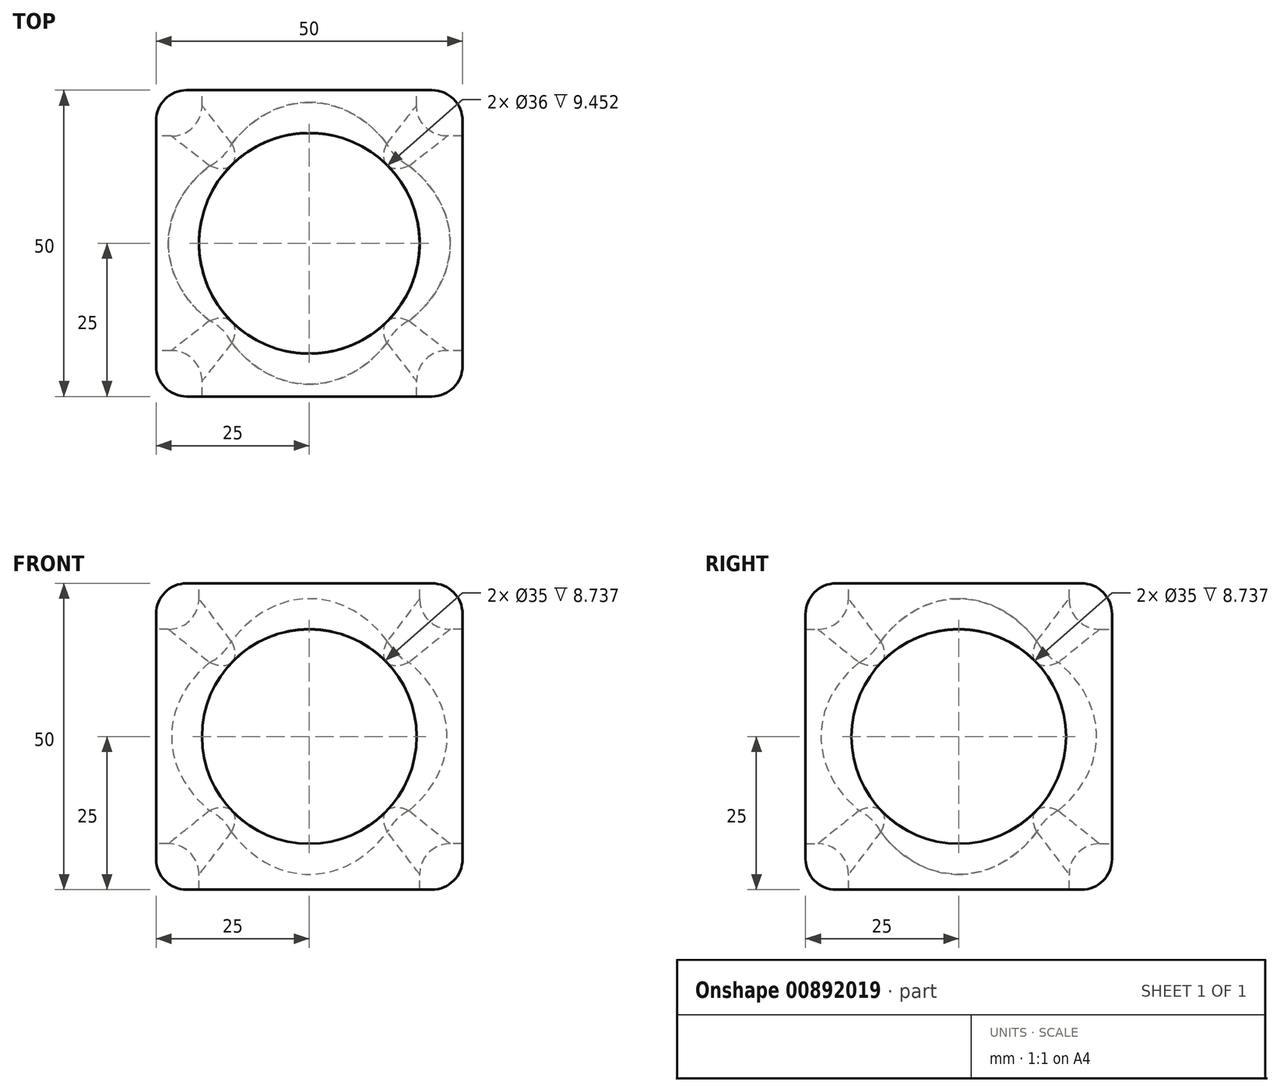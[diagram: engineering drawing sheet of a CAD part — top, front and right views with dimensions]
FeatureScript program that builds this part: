
annotation { "Feature Type Name" : "Feature", "Feature Type Description" : "" }
export const myFeature = defineFeature(function(context is Context, id is Id, definition is map)
    precondition{}
    {
        {
            var Q0;
            Q0=qCreatedBy(makeId("Top.planeOp"),FACE);
            var sketch = newSketch(context, id + "F0", { "sketchPlane" : qUnion([Q0])});
            skLineSegment(sketch, "E0.bottom", {"start": v(0, 0) * mm, "end": v(50, 0) * mm});
            skLineSegment(sketch, "E0.top", {"start": v(0, 50) * mm, "end": v(50, 50) * mm});
            skLineSegment(sketch, "E0.left", {"start": v(0, 0) * mm, "end": v(0, 50) * mm});
            skLineSegment(sketch, "E0.right", {"start": v(50, 0) * mm, "end": v(50, 50) * mm});
            skSolve(sketch);
        }
        {
            var Q0;
            Q0=makeQuery(id+"F0.imprint","IMPRINT",FACE,{"disambiguationData":[TD([[makeQuery(id+"F0.imprint","IMPRINT",EDGE,{"derivedFrom":sQuery(id+"F0.wireOp",EDGE,"E0.bottom")}),1.0]])]});
            extrude(context, id + "F1", {"entities" : qUnion([Q0]), "depth" : 50 * mm, "offsetDistance" : 25 * mm});
        }
        {
            var Q0;
            Q0=makeQuery(id+"F1.opExtrude","SWEPT_FACE",FACE,{"disambiguationData":[OSD([sQuery(id+"F0.wireOp",EDGE,"E0.top")])]});
            var Q1;
            Q1=makeQuery(id+"F1.opExtrude","SWEPT_EDGE",EDGE,{"disambiguationData":[OSD([sQuery(id+"F0.wireOp",EDGE,"E0.bottom"),sQuery(id+"F0.wireOp",EDGE,"E0.left")])]});
            var Q2;
            Q2=makeQuery(id+"F1.opExtrude","SWEPT_FACE",FACE,{"disambiguationData":[OSD([sQuery(id+"F0.wireOp",EDGE,"E0.bottom")])]});
            var Q3;
            Q3=makeQuery(id+"F1.opExtrude","CAP_FACE",FACE,{"disambiguationData":[OSD([sQuery(id+"F0.wireOp",EDGE,"E0.bottom"),sQuery(id+"F0.wireOp",EDGE,"E0.top"),sQuery(id+"F0.wireOp",EDGE,"E0.left"),sQuery(id+"F0.wireOp",EDGE,"E0.right")])],"isStart":true});
            var Q4;
            Q4=makeQuery(id+"F1.opExtrude","SWEPT_EDGE",EDGE,{"disambiguationData":[OSD([sQuery(id+"F0.wireOp",EDGE,"E0.top"),sQuery(id+"F0.wireOp",EDGE,"E0.left")])]});
            var Q5;
            Q5=makeQuery(id+"F1.opExtrude","CAP_FACE",FACE,{"disambiguationData":[OSD([sQuery(id+"F0.wireOp",EDGE,"E0.bottom"),sQuery(id+"F0.wireOp",EDGE,"E0.top"),sQuery(id+"F0.wireOp",EDGE,"E0.left"),sQuery(id+"F0.wireOp",EDGE,"E0.right")])],"isStart":false});
            var Q6;
            Q6=makeQuery(id+"F1.opExtrude","SWEPT_EDGE",EDGE,{"disambiguationData":[OSD([sQuery(id+"F0.wireOp",EDGE,"E0.top"),sQuery(id+"F0.wireOp",EDGE,"E0.right")])]});
            var Q7;
            Q7=makeQuery(id+"F1.opExtrude","SWEPT_FACE",FACE,{"disambiguationData":[OSD([sQuery(id+"F0.wireOp",EDGE,"E0.left")])]});
            var Q8;
            Q8=makeQuery(id+"F1.opExtrude","CAP_EDGE",EDGE,{"disambiguationData":[OSD([sQuery(id+"F0.wireOp",EDGE,"E0.bottom")])],"isStart":false});
            var Q9;
            Q9=makeQuery(id+"F1.opExtrude","SWEPT_FACE",FACE,{"disambiguationData":[OSD([sQuery(id+"F0.wireOp",EDGE,"E0.right")])]});
            var Q10;
            Q10=makeQuery(id+"F1.opExtrude","CAP_EDGE",EDGE,{"disambiguationData":[OSD([sQuery(id+"F0.wireOp",EDGE,"E0.top")])],"isStart":true});
            var Q11;
            Q11=makeQuery(id+"F1.opExtrude","CAP_EDGE",EDGE,{"disambiguationData":[OSD([sQuery(id+"F0.wireOp",EDGE,"E0.top")])],"isStart":false});
            var Q12;
            Q12=makeQuery(id+"F1.opExtrude","CAP_EDGE",EDGE,{"disambiguationData":[OSD([sQuery(id+"F0.wireOp",EDGE,"E0.right")])],"isStart":false});
            var Q13;
            Q13=makeQuery(id+"F1.opExtrude","SWEPT_EDGE",EDGE,{"disambiguationData":[OSD([sQuery(id+"F0.wireOp",EDGE,"E0.bottom"),sQuery(id+"F0.wireOp",EDGE,"E0.right")])]});
            var Q14;
            Q14=makeQuery(id+"F1.opExtrude","CAP_EDGE",EDGE,{"disambiguationData":[OSD([sQuery(id+"F0.wireOp",EDGE,"E0.bottom")])],"isStart":true});
            var Q15;
            Q15=makeQuery(id+"F1.opExtrude","CAP_EDGE",EDGE,{"disambiguationData":[OSD([sQuery(id+"F0.wireOp",EDGE,"E0.left")])],"isStart":true});
            var Q16;
            Q16=makeQuery(id+"F1.opExtrude","CAP_EDGE",EDGE,{"disambiguationData":[OSD([sQuery(id+"F0.wireOp",EDGE,"E0.left")])],"isStart":false});
            var Q17;
            Q17=makeQuery(id+"F1.opExtrude","CAP_EDGE",EDGE,{"disambiguationData":[OSD([sQuery(id+"F0.wireOp",EDGE,"E0.right")])],"isStart":true});
            fillet(context, id + "F2", {"entities" : qUnion([Q0, Q1, Q2, Q3, Q4, Q5, Q6, Q7, Q8, Q9, Q10, Q11, Q12, Q13, Q14, Q15, Q16, Q17]), "radius" : 5 * mm, "tangentPropagation" : true, "allowEdgeOverflow" : false});
        }
        {
            var Q0;
            Q0=makeQuery(id+"F1.opExtrude","SWEPT_FACE",FACE,{"disambiguationData":[OSD([sQuery(id+"F0.wireOp",EDGE,"E0.top")])]});
            var sketch = newSketch(context, id + "F3", { "sketchPlane" : qUnion([Q0])});
            skCircle(sketch, "E1", {"center": v(-25, 25) * mm, "radius": 17.5 * mm});
            skPoint(sketch, "E1.centerSnap0", {"position": v(-25, 5) * mm});
            skPoint(sketch, "E1.centerSnap1", {"position": v(-45, 25) * mm});
            skSolve(sketch);
        }
        {
            var Q0;
            Q0=makeQuery(id+"F1.opExtrude","SWEPT_FACE",FACE,{"disambiguationData":[OSD([sQuery(id+"F0.wireOp",EDGE,"E0.left")])]});
            var sketch = newSketch(context, id + "F4", { "sketchPlane" : qUnion([Q0])});
            skCircle(sketch, "E2", {"center": v(-25, 25) * mm, "radius": 17.5 * mm});
            skPoint(sketch, "E2.centerSnap0", {"position": v(-25, 5) * mm});
            skPoint(sketch, "E2.centerSnap1", {"position": v(-45, 25) * mm});
            skSolve(sketch);
        }
        {
            var Q0;
            Q0=makeQuery(id+"F1.opExtrude","CAP_FACE",FACE,{"disambiguationData":[OSD([sQuery(id+"F0.wireOp",EDGE,"E0.bottom"),sQuery(id+"F0.wireOp",EDGE,"E0.top"),sQuery(id+"F0.wireOp",EDGE,"E0.left"),sQuery(id+"F0.wireOp",EDGE,"E0.right")])],"isStart":false});
            var sketch = newSketch(context, id + "F5", { "sketchPlane" : qUnion([Q0])});
            skCircle(sketch, "E3", {"center": v(25, 25) * mm, "radius": 18 * mm});
            skPoint(sketch, "E3.centerSnap0", {"position": v(5, 25) * mm});
            skPoint(sketch, "E3.centerSnap1", {"position": v(25, 45) * mm});
            skSolve(sketch);
        }
        {
            var Q0;
            Q0=makeQuery(id+"F3.imprint","IMPRINT",FACE,{"disambiguationData":[TD([[makeQuery(id+"F3.imprint","IMPRINT",EDGE,{"derivedFrom":sQuery(id+"F3.wireOp",EDGE,"E1")}),1.0]])]});
            var Q1;
            Q1=makeQuery(id+"F1.opExtrude","SWEPT_FACE",FACE,{"disambiguationData":[OSD([sQuery(id+"F0.wireOp",EDGE,"E0.bottom")])]});
            extrude(context, id + "F6", {"entities" : qUnion([Q0]), "operationType" : NewBodyOperationType.REMOVE, "endBound" : BoundingType.UP_TO_SURFACE, "oppositeDirection" : true, "depth" : 25 * mm, "endBoundEntityFace" : qUnion([Q1]), "offsetDistance" : 25 * mm});
        }
        {
            var Q0;
            Q0=makeQuery(id+"F4.imprint","IMPRINT",FACE,{"disambiguationData":[TD([[makeQuery(id+"F4.imprint","IMPRINT",EDGE,{"derivedFrom":sQuery(id+"F4.wireOp",EDGE,"E2")}),1.0]])]});
            var Q1;
            Q1=makeQuery(id+"F1.opExtrude","SWEPT_FACE",FACE,{"disambiguationData":[OSD([sQuery(id+"F0.wireOp",EDGE,"E0.right")])]});
            extrude(context, id + "F7", {"entities" : qUnion([Q0]), "operationType" : NewBodyOperationType.REMOVE, "endBound" : BoundingType.UP_TO_SURFACE, "oppositeDirection" : true, "depth" : 25 * mm, "endBoundEntityFace" : qUnion([Q1]), "offsetDistance" : 25 * mm});
        }
        {
            var Q0;
            Q0=makeQuery(id+"F5.imprint","IMPRINT",FACE,{"disambiguationData":[TD([[makeQuery(id+"F5.imprint","IMPRINT",EDGE,{"derivedFrom":sQuery(id+"F5.wireOp",EDGE,"E3")}),1.0]])]});
            var sketch = newSketch(context, id + "F8", { "sketchPlane" : qUnion([Q0])});
            skSolve(sketch);
        }
        {
            var Q0;
            Q0=makeQuery(id+"F8.imprint","IMPRINT",FACE,{"disambiguationData":[TD([[makeQuery(id+"F8.imprint","IMPRINT",EDGE,{"derivedFrom":makeQuery(id+"F5.imprint","IMPRINT",EDGE,{"derivedFrom":sQuery(id+"F5.wireOp",EDGE,"E3")})}),1.0]])]});
            var Q1;
            Q1=makeQuery(id+"F1.opExtrude","CAP_FACE",FACE,{"disambiguationData":[OSD([sQuery(id+"F0.wireOp",EDGE,"E0.bottom"),sQuery(id+"F0.wireOp",EDGE,"E0.top"),sQuery(id+"F0.wireOp",EDGE,"E0.left"),sQuery(id+"F0.wireOp",EDGE,"E0.right")])],"isStart":true});
            extrude(context, id + "F9", {"entities" : qUnion([Q0]), "operationType" : NewBodyOperationType.REMOVE, "endBound" : BoundingType.UP_TO_SURFACE, "oppositeDirection" : true, "depth" : 25 * mm, "endBoundEntityFace" : qUnion([Q1]), "offsetDistance" : 25 * mm});
        }
        {
            var Q0;
            Q0=makeQuery(id+"F7.boolean.opBoolean","INTERSECT",EDGE,{"disambiguationData":[OD(0.0)],"derivedFrom":[makeQuery(id+"F6.boolean.opBoolean","COPY",FACE,{"derivedFrom":makeQuery(id+"F6.opExtrude","SWEPT_FACE",FACE,{"disambiguationData":[OSD([sQuery(id+"F3.wireOp",EDGE,"E1")])]})}),makeQuery(id+"F7.opExtrude","SWEPT_FACE",FACE,{"disambiguationData":[OSD([sQuery(id+"F4.wireOp",EDGE,"E2")])]})]});
            var Q1;
            {var subQ0=makeQuery(id+"F7.opExtrude","SWEPT_FACE",FACE,{"disambiguationData":[OSD([sQuery(id+"F4.wireOp",EDGE,"E2")])]});Q1=makeQuery(id+"F9.boolean.opBoolean","INTERSECT",EDGE,{"disambiguationData":[OD(1.0)],"derivedFrom":[makeQuery(id+"F7.boolean.opBoolean","COPY",FACE,{"disambiguationData":[TD([makeQuery(id+"F1.opExtrude","SWEPT_FACE",FACE,{"disambiguationData":[OSD([sQuery(id+"F0.wireOp",EDGE,"E0.left")])]})])],"derivedFrom":subQ0}),makeQuery(id+"F9.opExtrude","SWEPT_FACE",FACE,{"disambiguationData":[OSD([sQuery(id+"F5.wireOp",EDGE,"E3")])]})]});}
            var Q2;
            {var subQ0=makeQuery(id+"F6.boolean.opBoolean","COPY",FACE,{"derivedFrom":makeQuery(id+"F6.opExtrude","SWEPT_FACE",FACE,{"disambiguationData":[OSD([sQuery(id+"F3.wireOp",EDGE,"E1")])]})});Q2=makeQuery(id+"F9.boolean.opBoolean","INTERSECT",EDGE,{"disambiguationData":[OD(1.0)],"derivedFrom":[makeQuery(id+"F7.boolean.opBoolean","SPLIT",FACE,{"disambiguationData":[TD([makeQuery(id+"F1.opExtrude","SWEPT_FACE",FACE,{"disambiguationData":[OSD([sQuery(id+"F0.wireOp",EDGE,"E0.top")])]})])],"derivedFrom":subQ0}),makeQuery(id+"F9.opExtrude","SWEPT_FACE",FACE,{"disambiguationData":[OSD([sQuery(id+"F5.wireOp",EDGE,"E3")])]})]});}
            var Q3;
            {var subQ0=makeQuery(id+"F6.boolean.opBoolean","COPY",FACE,{"derivedFrom":makeQuery(id+"F6.opExtrude","SWEPT_FACE",FACE,{"disambiguationData":[OSD([sQuery(id+"F3.wireOp",EDGE,"E1")])]})});Q3=makeQuery(id+"F9.boolean.opBoolean","INTERSECT",EDGE,{"disambiguationData":[OD(1.0)],"derivedFrom":[makeQuery(id+"F7.boolean.opBoolean","SPLIT",FACE,{"disambiguationData":[TD([makeQuery(id+"F1.opExtrude","SWEPT_FACE",FACE,{"disambiguationData":[OSD([sQuery(id+"F0.wireOp",EDGE,"E0.bottom")])]})])],"derivedFrom":subQ0}),makeQuery(id+"F9.opExtrude","SWEPT_FACE",FACE,{"disambiguationData":[OSD([sQuery(id+"F5.wireOp",EDGE,"E3")])]})]});}
            var Q4;
            Q4=makeQuery(id+"F7.boolean.opBoolean","INTERSECT",EDGE,{"disambiguationData":[OD(3.0)],"derivedFrom":[makeQuery(id+"F6.boolean.opBoolean","COPY",FACE,{"derivedFrom":makeQuery(id+"F6.opExtrude","SWEPT_FACE",FACE,{"disambiguationData":[OSD([sQuery(id+"F3.wireOp",EDGE,"E1")])]})}),makeQuery(id+"F7.opExtrude","SWEPT_FACE",FACE,{"disambiguationData":[OSD([sQuery(id+"F4.wireOp",EDGE,"E2")])]})]});
            var Q5;
            {var subQ0=makeQuery(id+"F7.opExtrude","SWEPT_FACE",FACE,{"disambiguationData":[OSD([sQuery(id+"F4.wireOp",EDGE,"E2")])]});Q5=makeQuery(id+"F9.boolean.opBoolean","INTERSECT",EDGE,{"disambiguationData":[OD(1.0)],"derivedFrom":[makeQuery(id+"F7.boolean.opBoolean","COPY",FACE,{"disambiguationData":[TD([makeQuery(id+"F1.opExtrude","SWEPT_FACE",FACE,{"disambiguationData":[OSD([sQuery(id+"F0.wireOp",EDGE,"E0.right")])]})])],"derivedFrom":subQ0}),makeQuery(id+"F9.opExtrude","SWEPT_FACE",FACE,{"disambiguationData":[OSD([sQuery(id+"F5.wireOp",EDGE,"E3")])]})]});}
            var Q6;
            {var subQ0=makeQuery(id+"F7.opExtrude","SWEPT_FACE",FACE,{"disambiguationData":[OSD([sQuery(id+"F4.wireOp",EDGE,"E2")])]});Q6=makeQuery(id+"F9.boolean.opBoolean","INTERSECT",EDGE,{"disambiguationData":[OD(0.0)],"derivedFrom":[makeQuery(id+"F7.boolean.opBoolean","COPY",FACE,{"disambiguationData":[TD([makeQuery(id+"F1.opExtrude","SWEPT_FACE",FACE,{"disambiguationData":[OSD([sQuery(id+"F0.wireOp",EDGE,"E0.right")])]})])],"derivedFrom":subQ0}),makeQuery(id+"F9.opExtrude","SWEPT_FACE",FACE,{"disambiguationData":[OSD([sQuery(id+"F5.wireOp",EDGE,"E3")])]})]});}
            var Q7;
            {var subQ0=makeQuery(id+"F6.boolean.opBoolean","COPY",FACE,{"derivedFrom":makeQuery(id+"F6.opExtrude","SWEPT_FACE",FACE,{"disambiguationData":[OSD([sQuery(id+"F3.wireOp",EDGE,"E1")])]})});Q7=makeQuery(id+"F9.boolean.opBoolean","INTERSECT",EDGE,{"disambiguationData":[OD(0.0)],"derivedFrom":[makeQuery(id+"F7.boolean.opBoolean","SPLIT",FACE,{"disambiguationData":[TD([makeQuery(id+"F1.opExtrude","SWEPT_FACE",FACE,{"disambiguationData":[OSD([sQuery(id+"F0.wireOp",EDGE,"E0.top")])]})])],"derivedFrom":subQ0}),makeQuery(id+"F9.opExtrude","SWEPT_FACE",FACE,{"disambiguationData":[OSD([sQuery(id+"F5.wireOp",EDGE,"E3")])]})]});}
            var Q8;
            Q8=makeQuery(id+"F7.boolean.opBoolean","INTERSECT",EDGE,{"disambiguationData":[OD(1.0)],"derivedFrom":[makeQuery(id+"F6.boolean.opBoolean","COPY",FACE,{"derivedFrom":makeQuery(id+"F6.opExtrude","SWEPT_FACE",FACE,{"disambiguationData":[OSD([sQuery(id+"F3.wireOp",EDGE,"E1")])]})}),makeQuery(id+"F7.opExtrude","SWEPT_FACE",FACE,{"disambiguationData":[OSD([sQuery(id+"F4.wireOp",EDGE,"E2")])]})]});
            var Q9;
            {var subQ0=makeQuery(id+"F6.boolean.opBoolean","COPY",FACE,{"derivedFrom":makeQuery(id+"F6.opExtrude","SWEPT_FACE",FACE,{"disambiguationData":[OSD([sQuery(id+"F3.wireOp",EDGE,"E1")])]})});Q9=makeQuery(id+"F9.boolean.opBoolean","INTERSECT",EDGE,{"disambiguationData":[OD(0.0)],"derivedFrom":[makeQuery(id+"F7.boolean.opBoolean","SPLIT",FACE,{"disambiguationData":[TD([makeQuery(id+"F1.opExtrude","SWEPT_FACE",FACE,{"disambiguationData":[OSD([sQuery(id+"F0.wireOp",EDGE,"E0.bottom")])]})])],"derivedFrom":subQ0}),makeQuery(id+"F9.opExtrude","SWEPT_FACE",FACE,{"disambiguationData":[OSD([sQuery(id+"F5.wireOp",EDGE,"E3")])]})]});}
            var Q10;
            {var subQ0=makeQuery(id+"F7.opExtrude","SWEPT_FACE",FACE,{"disambiguationData":[OSD([sQuery(id+"F4.wireOp",EDGE,"E2")])]});Q10=makeQuery(id+"F9.boolean.opBoolean","INTERSECT",EDGE,{"disambiguationData":[OD(0.0)],"derivedFrom":[makeQuery(id+"F7.boolean.opBoolean","COPY",FACE,{"disambiguationData":[TD([makeQuery(id+"F1.opExtrude","SWEPT_FACE",FACE,{"disambiguationData":[OSD([sQuery(id+"F0.wireOp",EDGE,"E0.left")])]})])],"derivedFrom":subQ0}),makeQuery(id+"F9.opExtrude","SWEPT_FACE",FACE,{"disambiguationData":[OSD([sQuery(id+"F5.wireOp",EDGE,"E3")])]})]});}
            var Q11;
            Q11=makeQuery(id+"F7.boolean.opBoolean","INTERSECT",EDGE,{"disambiguationData":[OD(2.0)],"derivedFrom":[makeQuery(id+"F6.boolean.opBoolean","COPY",FACE,{"derivedFrom":makeQuery(id+"F6.opExtrude","SWEPT_FACE",FACE,{"disambiguationData":[OSD([sQuery(id+"F3.wireOp",EDGE,"E1")])]})}),makeQuery(id+"F7.opExtrude","SWEPT_FACE",FACE,{"disambiguationData":[OSD([sQuery(id+"F4.wireOp",EDGE,"E2")])]})]});
            var Q12;
            Q12=makeQuery(id+"F9.boolean.opBoolean","COPY",EDGE,{"derivedFrom":makeQuery(id+"F9.opExtrude","CAP_EDGE",EDGE,{"disambiguationData":[OSD([sQuery(id+"F5.wireOp",EDGE,"E3")])],"isStart":false})});
            var Q13;
            Q13=makeQuery(id+"F7.boolean.opBoolean","COPY",EDGE,{"derivedFrom":makeQuery(id+"F7.opExtrude","CAP_EDGE",EDGE,{"disambiguationData":[OSD([sQuery(id+"F4.wireOp",EDGE,"E2")])],"isStart":false})});
            var Q14;
            Q14=makeQuery(id+"F9.boolean.opBoolean","COPY",EDGE,{"derivedFrom":makeQuery(id+"F9.opExtrude","CAP_EDGE",EDGE,{"disambiguationData":[OSD([sQuery(id+"F5.wireOp",EDGE,"E3")])],"isStart":true})});
            var Q15;
            Q15=makeQuery(id+"F7.boolean.opBoolean","COPY",EDGE,{"derivedFrom":makeQuery(id+"F7.opExtrude","CAP_EDGE",EDGE,{"disambiguationData":[OSD([sQuery(id+"F4.wireOp",EDGE,"E2")])],"isStart":true})});
            var Q16;
            Q16=makeQuery(id+"F6.boolean.opBoolean","COPY",EDGE,{"derivedFrom":makeQuery(id+"F6.opExtrude","CAP_EDGE",EDGE,{"disambiguationData":[OSD([sQuery(id+"F3.wireOp",EDGE,"E1")])],"isStart":false})});
            var Q17;
            Q17=makeQuery(id+"F6.boolean.opBoolean","COPY",EDGE,{"derivedFrom":makeQuery(id+"F6.opExtrude","CAP_EDGE",EDGE,{"disambiguationData":[OSD([sQuery(id+"F3.wireOp",EDGE,"E1")])],"isStart":true})});
            fillet(context, id + "F10", {"entities" : qUnion([Q0, Q1, Q2, Q3, Q4, Q5, Q6, Q7, Q8, Q9, Q10, Q11, Q12, Q13, Q14, Q15, Q16, Q17]), "radius" : 5 * mm, "tangentPropagation" : true, "allowEdgeOverflow" : false});
        }
    });
